# Revit family: QF_MACOM_SAL_2MA
name_source: partatom
category: Equipamento especial
units: mm (PartAtom-declared; Revit-internal decimal feet)

## family parameters
Com base no plano de trabalho = Não
Compartilhado = Não
Corte com vazios quando carregada = Não
Cota do conector redondo = Utilizar diâmetro
Número OmniClass = 23.40.40.14.17.11
Ponto de cálculo do ambiente = Não
Sempre na vertical = Sim
Tipo de parte = Normal
Título OmniClass = Cookers, Ovens, Stoves

## types (1)
- SAL-2MA
    Capacity = 01 GN 1/1
    Cycle = 60 Hz
    Degree of Protection = IP 22
    Depth = 425,000 mm
    Descrição = SALAMANDRA ELETRICA MACOM
    Elec Connection Height = 101,000 mm
    Electric Power = 1700 W
    Elevação padrão = 0,000 mm
    Fabricante = MACOM
    Height = 421,000 mm
    Modelo = SAL-2MA
    Show Logo = Sim
    URL = https://www.acosmacom.com.br
    Volts = 220 V
    Volume = 0,13 m³
    Weight = 22,00 kg
    Width = 711,000 mm

## geometry (parser evidence)
native form markers: Sweep x10
no freeform markers — native parametric forms only
